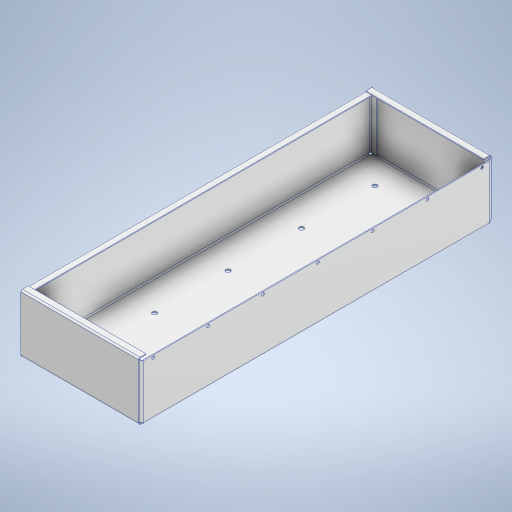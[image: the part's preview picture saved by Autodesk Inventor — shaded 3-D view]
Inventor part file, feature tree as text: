
AUTODESK INVENTOR PART (.ipt)
format: ipt  version: 2023 (Build 270158000, 158)  size: 489,984 bytes
history: native  units: in
note: dims shown in document units (in); Inventor stores cm internally (conversion verified against a paired STEP export)
features: sheet_metal_op x16, sketch x12, other x10, hole x2, pattern_linear x2
ambient origin geometry x8: Origin, YZ Plane, XZ Plane, XY Plane, X Axis, Y Axis, Z Axis, Center Point
bodies: Solid1 (feature_tree)
feature tree (42):
  sheet_metal_op  "Face1"
  hole  "Hole1"  [1 undecoded]
  pattern_linear  "Rectangular Pattern1"  Count1=30  [1 undecoded]
  sheet_metal_op  "Flange4"
  sheet_metal_op  "Flange5"
  sheet_metal_op  "Flange11"
  sketch  "Sketch21"  dims[d51=0.0312in]
  hole  "Hole2"  [1 undecoded]
  pattern_linear  "Rectangular Pattern2"  Count1=5  [1 undecoded]
  sheet_metal_op  "Flange14"
  sheet_metal_op  "Flange17"
  sketch  "Sketch1"  dims[d0=23.622in d1=7.874in d2=11.811in]
  other  "Plate1"
  sketch  "Sketch2"  dims[d3=3.937in d4=0.0625in]
  sketch  "Sketch6"  dims[d5=0.2969in d6=0.2953in d7=0.1476in d8=0.0984in d9=90.0deg d10=0.0625in]
  other  "Plate5"
  sheet_metal_op  "Bend4"
  sheet_metal_op  "Corner4"
  sketch  "Sketch7"  dims[d11=0.0in d12=1.9685in]
  other  "Plate6"
  sheet_metal_op  "Bend5"
  sheet_metal_op  "Corner5"
  sketch  "Sketch8"  dims[d13=2.0669in]
  sketch  "Sketch9"  dims[d14=0.7874in d16=3.937in]
  sketch  "Sketch17"  dims[d17=1.9685in d19=4.9213in]
  other  "Plate12"
  sheet_metal_op  "Bend11"
  sheet_metal_op  "Corner11"
  sketch  "Sketch20"  dims[d50=0.0625in]
  sketch  "Sketch22"  dims[d52=0.125in]
  sketch  "Sketch23"  dims[d53=0.0625in]
  other  "Plate15"
  sheet_metal_op  "Bend14"
  sheet_metal_op  "Corner14"
  sketch  "Sketch26"  dims[d54=3.8465in d55=90.0deg d56=0.0787in d57=0.25in d58=0.0625in d59=0.0625in d60=0.0625in d61=0.0312in d62=0.125in d63=0.0625in d64=3.937in d65=90.0deg d66=0.0787in d67=0.25in d68=0.0625in d69=0.0625in d70=0.0in d71=0.0in d72=0.0in d73=0.0in d78=0.0625in d79=0.0in d80=0.0625in d81=0.0in d147=0.0625in d148=0.0312in d149=0.125in d150=0.0625in d151=0.5in d152=90.0deg d153=0.0787in d154=0.25in d155=0.0625in d156=0.0625in d177=0.194in d178=0.2953in d179=0.1476in d180=0.0984in d181=90.0deg d182=0.0625in d183=0.8108in d185=0.6289in d186=2.7559in d188=3.6755in d190=0.0625in d191=0.0in d192=0.162in d193=0.2073in d195=0.0625in d196=0.0in d197=0.1in d198=0.0625in d199=0.0312in d200=0.125in d201=0.0625in d202=0.5in d203=90.0deg d204=0.0591in d205=0.25in d206=0.0625in d207=0.0625in d228=0.0625in d229=0.0312in d230=0.125in d231=0.0625in d232=0.5in d233=90.0deg d234=0.0394in d235=0.25in d236=0.0625in d237=0.0625in d238=0.1969in d239=0.1969in d240=0.1662in d241=0.1662in]
  other  "Plate18"
  sheet_metal_op  "Bend17"
  sheet_metal_op  "Corner17"
  other  "Cut2"
  other  "Cut3"
  other  "Cut4"
  other  "Cut5"
note: 4 required parameter values undecoded (feature->parameter linkage not recoverable at this tier; creation-order binding heuristic only, values carry confidence <= 0.55)
